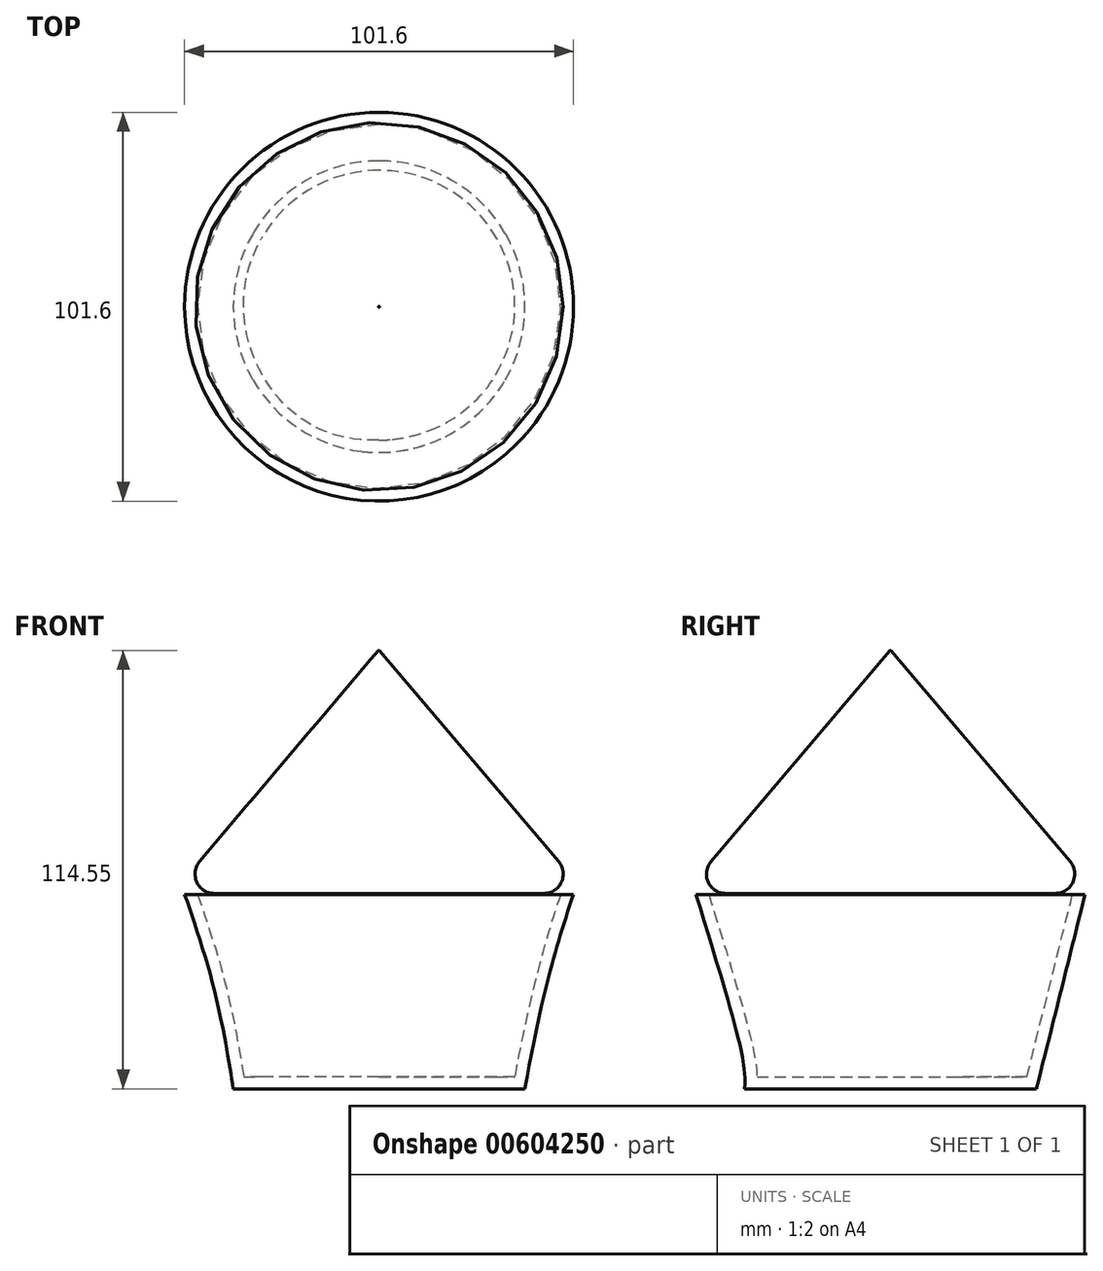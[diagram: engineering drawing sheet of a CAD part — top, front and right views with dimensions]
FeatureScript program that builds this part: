
annotation { "Feature Type Name" : "Feature", "Feature Type Description" : "" }
export const myFeature = defineFeature(function(context is Context, id is Id, definition is map)
    precondition{}
    {
        {
            var Q0;
            Q0=qCreatedBy(makeId("Top.planeOp"),FACE);
            var sketch = newSketch(context, id + "F0", { "sketchPlane" : qUnion([Q0])});
            skCircle(sketch, "E0", {"center": v(0, 0) * mm, "radius": 38.1 * mm});
            skSolve(sketch);
        }
        {
            var Q0;
            Q0=makeQuery(id+"F0.imprint","IMPRINT",FACE,{"disambiguationData":[TD([[makeQuery(id+"F0.imprint","IMPRINT",EDGE,{"derivedFrom":sQuery(id+"F0.wireOp",EDGE,"E0")}),1.0]])]});
            cPlane(context, id + "F1", {"entities" : qUnion([Q0]), "cplaneType" : CPlaneType.OFFSET, "offset" : 50.8 * mm, "width" : 152.4 * mm, "height" : 152.4 * mm});
        }
        {
            var Q0;
            Q0=qCreatedBy(id+"F1.planeOp",FACE);
            var sketch = newSketch(context, id + "F2", { "sketchPlane" : qUnion([Q0])});
            skCircle(sketch, "E1", {"center": v(0, 0) * mm, "radius": 50.8 * mm});
            skLineSegment(sketch, "E2", {"start": v(0, 50.8) * mm, "end": v(0, 0) * mm});
            skLineSegment(sketch, "E3", {"start": v(-50.8, 0) * mm, "end": v(50.8, 0) * mm});
            skPoint(sketch, "E4", {"position": v(0, 33.87) * mm});
            skPoint(sketch, "E5", {"position": v(0, 16.93) * mm});
            skPoint(sketch, "E6", {"position": v(16.93, 0) * mm});
            skPoint(sketch, "E7", {"position": v(33.87, 0) * mm});
            skPoint(sketch, "E8.MirrorP", {"position": v(0, -16.93) * mm});
            skPoint(sketch, "E9.MirrorP", {"position": v(0, -33.87) * mm});
            skPoint(sketch, "E10.MirrorP", {"position": v(-16.93, 0) * mm});
            skPoint(sketch, "E11.MirrorP", {"position": v(-33.87, 0) * mm});
            skLineSegment(sketch, "E12", {"start": v(0, 0) * mm, "end": v(35.92, -35.92) * mm});
            skLineSegment(sketch, "E13", {"start": v(0, 0) * mm, "end": v(35.92, 35.92) * mm});
            skLineSegment(sketch, "E14.MirrorCS", {"start": v(0, 0) * mm, "end": v(-35.92, 35.92) * mm});
            skPoint(sketch, "E15", {"position": v(11.97, 11.97) * mm});
            skPoint(sketch, "E16", {"position": v(23.95, 23.95) * mm});
            skPoint(sketch, "E17", {"position": v(13.93, -13.93) * mm});
            skPoint(sketch, "E18", {"position": v(18.99, -18.99) * mm});
            skSolve(sketch);
        }
        {
            var Q0;
            Q0=makeQuery(id+"F0.imprint","IMPRINT",FACE,{"disambiguationData":[TD([[makeQuery(id+"F0.imprint","IMPRINT",EDGE,{"derivedFrom":sQuery(id+"F0.wireOp",EDGE,"E0")}),1.0]])]});
            var Q1;
            Q1=makeQuery(id+"F2.imprint","IMPRINT",FACE,{"disambiguationData":[TD([[makeQuery(id+"F2.imprint","IMPRINT",EDGE,{"derivedFrom":sQuery(id+"F2.wireOp",EDGE,"E1")}),1.0]])]});
            loft(context, id + "F3", {"sheetProfilesArray" : [{ "sheetProfileEntities" : qUnion([Q0]) }, { "sheetProfileEntities" : qUnion([Q1]) }]});
        }
        {
            var Q0;
            Q0=makeQuery(id+"F3.opLoft","CAP_FACE",FACE,{"disambiguationData":[OSD([makeQuery(id+"F2.imprint","IMPRINT",FACE,{"disambiguationData":[TD([[makeQuery(id+"F2.imprint","IMPRINT",EDGE,{"derivedFrom":sQuery(id+"F2.wireOp",EDGE,"E1")}),1.0]])]})])],"isStart":true});
            shell(context, id + "F4", {"entities" : qUnion([Q0]), "thickness" : 3.17 * mm});
        }
        {
            var Q0;
            Q0=qCreatedBy(id+"F1.planeOp",FACE);
            cPlane(context, id + "F5", {"entities" : qUnion([Q0]), "cplaneType" : CPlaneType.OFFSET, "offset" : 0.25 * mm, "width" : 152.4 * mm, "height" : 152.4 * mm});
        }
        {
            var Q0;
            Q0=qCreatedBy(id+"F5.planeOp",FACE);
            var sketch = newSketch(context, id + "F6", { "sketchPlane" : qUnion([Q0])});
            skCircle(sketch, "E19", {"center": v(0, 0) * mm, "radius": 53.98 * mm});
            skSolve(sketch);
        }
        {
            var Q0;
            Q0=qCreatedBy(id+"F5.planeOp",FACE);
            cPlane(context, id + "F7", {"entities" : qUnion([Q0]), "cplaneType" : CPlaneType.OFFSET, "offset" : 63.5 * mm, "width" : 152.4 * mm, "height" : 152.4 * mm});
        }
        {
            var Q0;
            Q0=qCreatedBy(id+"F7.planeOp",FACE);
            var sketch = newSketch(context, id + "F8", { "sketchPlane" : qUnion([Q0])});
            skCircle(sketch, "E20.0", {"center": v(0, 0) * mm, "radius": 0.13 * mm});
            skSolve(sketch);
        }
        {
            var Q0;
            Q0 = qSketchRegion(id + "F8", true);
            var Q1;
            Q1 = qSketchRegion(id + "F6", true);
            loft(context, id + "F9", {"sheetProfilesArray" : [{ "sheetProfileEntities" : qUnion([Q0]) }, { "sheetProfileEntities" : qUnion([Q1]) }]});
        }
        {
            var Q0;
            Q0=makeQuery(id+"F9.opLoft","MID_CAP_EDGE",EDGE,{"disambiguationData":[OSD([sQuery(id+"F6.wireOp",EDGE,"E19"),sQuery(id+"F8.wireOp",EDGE,"E20.0")])],"capPos":1.0});
            fillet(context, id + "F10", {"entities" : qUnion([Q0]), "radius" : 5.08 * mm, "tangentPropagation" : true, "allowEdgeOverflow" : false});
        }
    });
